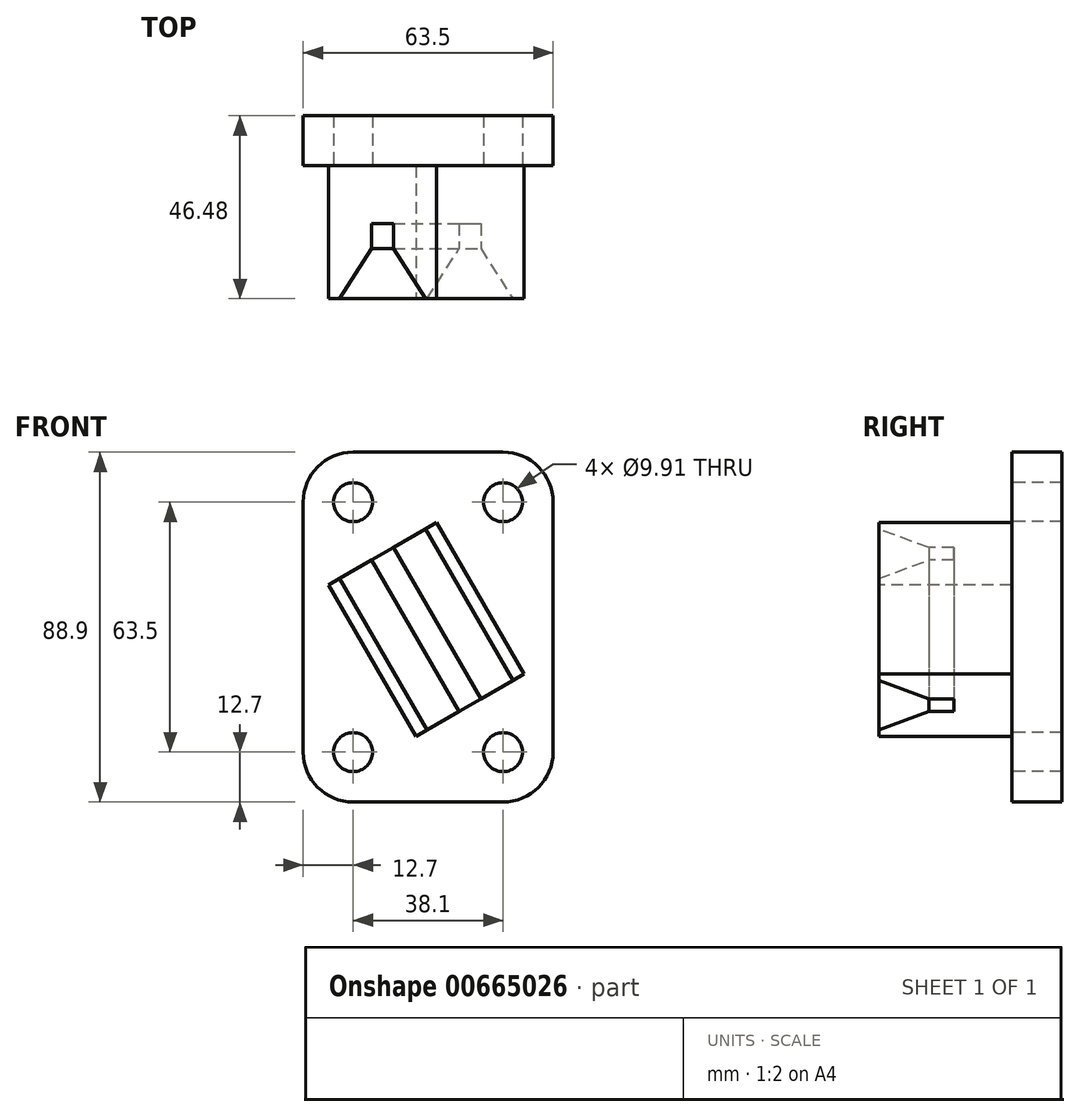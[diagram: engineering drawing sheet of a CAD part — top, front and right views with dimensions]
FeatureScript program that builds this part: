
annotation { "Feature Type Name" : "Feature", "Feature Type Description" : "" }
export const myFeature = defineFeature(function(context is Context, id is Id, definition is map)
    precondition{}
    {
        {
            var Q0;
            Q0=qCreatedBy(makeId("Front.planeOp"),FACE);
            var sketch = newSketch(context, id + "F0", { "sketchPlane" : qUnion([Q0])});
            skLineSegment(sketch, "E0", {"start": v(12.7, 0) * mm, "end": v(50.8, 0) * mm});
            skLineSegment(sketch, "E1", {"start": v(63.5, 12.7) * mm, "end": v(63.5, 76.2) * mm});
            skLineSegment(sketch, "E2", {"start": v(50.8, 88.9) * mm, "end": v(12.7, 88.9) * mm});
            skLineSegment(sketch, "E3", {"start": v(0, 76.2) * mm, "end": v(0, 12.7) * mm});
            skPoint(sketch, "E4.visualSharp", {"position": v(0, 88.9) * mm});
            skArc(sketch, "E4.filletArc", {"start": v(12.7, 88.9) * mm, "mid": v(3.72, 85.18) * mm, "end": v(0, 76.2) * mm});
            skPoint(sketch, "E5.visualSharp", {"position": v(63.5, 88.9) * mm});
            skArc(sketch, "E5.filletArc", {"start": v(63.5, 76.2) * mm, "mid": v(59.78, 85.18) * mm, "end": v(50.8, 88.9) * mm});
            skPoint(sketch, "E6.visualSharp", {"position": v(63.5, 0) * mm});
            skArc(sketch, "E6.filletArc", {"start": v(50.8, 0) * mm, "mid": v(59.78, 3.72) * mm, "end": v(63.5, 12.7) * mm});
            skPoint(sketch, "E7.visualSharp", {"position": v(0, 0) * mm});
            skArc(sketch, "E7.filletArc", {"start": v(0, 12.7) * mm, "mid": v(3.72, 3.72) * mm, "end": v(12.7, 0) * mm});
            skCircle(sketch, "E8", {"center": v(12.7, 76.2) * mm, "radius": 4.95 * mm});
            skCircle(sketch, "E9", {"center": v(50.8, 76.2) * mm, "radius": 4.95 * mm});
            skCircle(sketch, "E10", {"center": v(12.7, 12.7) * mm, "radius": 4.95 * mm});
            skCircle(sketch, "E11", {"center": v(50.8, 12.7) * mm, "radius": 4.95 * mm});
            skLineSegment(sketch, "E12", {"start": v(63.5, 12.7) * mm, "end": v(63.5, 45.21) * mm});
            skLineSegment(sketch, "E13", {"start": v(63.5, 0) * mm, "end": v(63.5, 32.51) * mm});
            skLineSegment(sketch, "E14", {"start": v(56.13, 32.51) * mm, "end": v(33.9, 71) * mm});
            skLineSegment(sketch, "E15.0", {"start": v(28.64, 16.64) * mm, "end": v(6.41, 55.13) * mm});
            skLineSegment(sketch, "E16", {"start": v(33.9, 71) * mm, "end": v(6.41, 55.13) * mm});
            skLineSegment(sketch, "E17", {"start": v(28.64, 16.64) * mm, "end": v(56.13, 32.51) * mm});
            skSolve(sketch);
        }
        {
            var Q0;
            Q0=makeQuery(id+"F0.imprint","IMPRINT",FACE,{"disambiguationData":[TD([[makeQuery(id+"F0.imprint","IMPRINT",EDGE,{"derivedFrom":sQuery(id+"F0.wireOp",EDGE,"E0")}),1.0]])]});
            var Q1;
            Q1=makeQuery(id+"F0.imprint","IMPRINT",FACE,{"disambiguationData":[TD([[makeQuery(id+"F0.imprint","IMPRINT",EDGE,{"derivedFrom":sQuery(id+"F0.wireOp",EDGE,"E14")}),1.0]])]});
            extrude(context, id + "F1", {"entities" : qUnion([Q0, Q1]), "oppositeDirection" : true, "depth" : 12.7 * mm, "offsetDistance" : 25.4 * mm});
        }
        {
            var Q0;
            Q0=sQuery(id+"F0.wireOp",VERTEX,"E15.0.start");
            var Q1;
            Q1=sQuery(id+"F0.wireOp",EDGE,"E15.0");
            cPlane(context, id + "F2", {"entities" : qUnion([Q0, Q1]), "cplaneType" : CPlaneType.LINE_POINT, "offset" : 25.4 * mm, "width" : 152.4 * mm, "height" : 152.4 * mm});
        }
        {
            var Q0;
            Q0=qCreatedBy(id+"F2.planeOp",FACE);
            var sketch = newSketch(context, id + "F3", { "sketchPlane" : qUnion([Q0])});
            skLineSegment(sketch, "E18.0", {"start": v(33.12, 0) * mm, "end": v(64.87, 0) * mm});
            skLineSegment(sketch, "E19", {"start": v(33.12, 0) * mm, "end": v(33.12, -33.78) * mm});
            skLineSegment(sketch, "E20", {"start": v(33.12, -33.78) * mm, "end": v(36.42, -33.78) * mm});
            skLineSegment(sketch, "E21", {"start": v(64.87, 0) * mm, "end": v(64.87, -33.78) * mm});
            skLineSegment(sketch, "E22", {"start": v(64.87, -33.78) * mm, "end": v(61.57, -33.78) * mm});
            skLineSegment(sketch, "E23", {"start": v(33.12, -33.78) * mm, "end": v(33.12, -14.73) * mm});
            skLineSegment(sketch, "E24", {"start": v(45.82, -14.73) * mm, "end": v(52.17, -14.73) * mm});
            skLineSegment(sketch, "E25", {"start": v(49, -14.73) * mm, "end": v(45.82, -14.73) * mm});
            skLineSegment(sketch, "E26", {"start": v(45.82, -14.73) * mm, "end": v(45.82, -21.08) * mm});
            skLineSegment(sketch, "E27", {"start": v(49, -14.73) * mm, "end": v(52.17, -14.73) * mm});
            skLineSegment(sketch, "E28", {"start": v(52.17, -14.73) * mm, "end": v(52.17, -21.08) * mm});
            skPoint(sketch, "E29.end.orphan", {"position": v(49, 0) * mm});
            skPoint(sketch, "E30.orphan", {"position": v(64.87, -14.73) * mm});
            skLineSegment(sketch, "E31", {"start": v(36.42, -33.78) * mm, "end": v(45.82, -21.08) * mm});
            skLineSegment(sketch, "E32", {"start": v(52.17, -21.08) * mm, "end": v(61.57, -33.78) * mm});
            skSolve(sketch);
        }
        {
            var Q0;
            Q0=makeQuery(id+"F3.imprint","IMPRINT",FACE,{"disambiguationData":[TD([[makeQuery(id+"F3.imprint","IMPRINT",EDGE,{"derivedFrom":sQuery(id+"F3.wireOp",EDGE,"E18.0")}),-1.0]])]});
            var Q1;
            Q1=sQuery(id+"F0.wireOp",VERTEX,"E15.0.end");
            extrude(context, id + "F4", {"entities" : qUnion([Q0]), "operationType" : NewBodyOperationType.ADD, "endBound" : BoundingType.UP_TO_VERTEX, "depth" : 25.4 * mm, "endBoundEntityVertex" : qUnion([Q1]), "offsetDistance" : 25.4 * mm});
        }
    });
